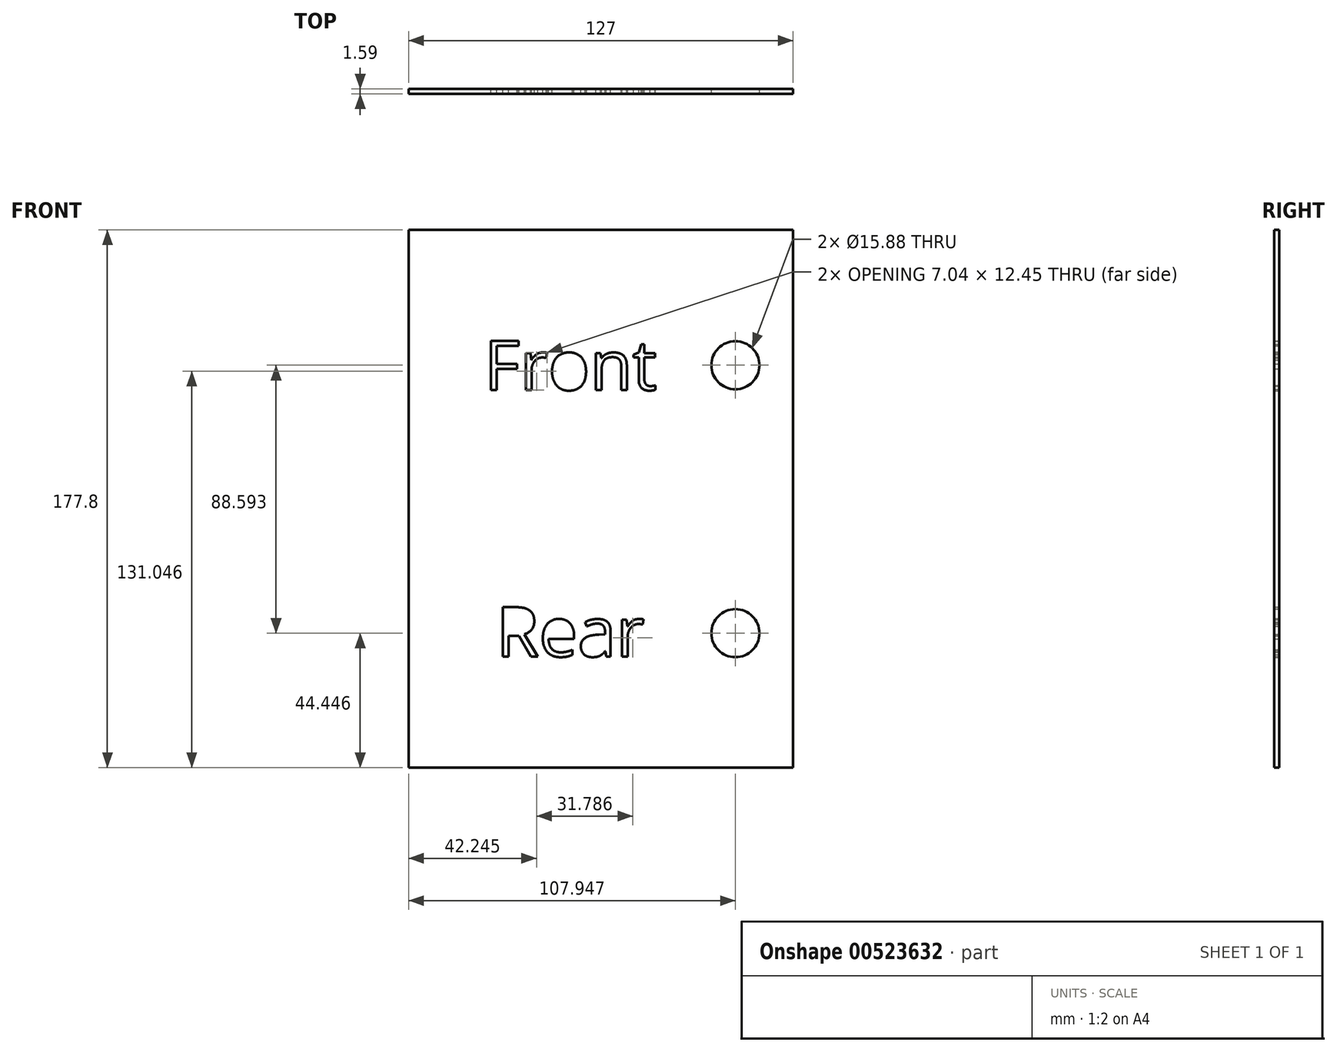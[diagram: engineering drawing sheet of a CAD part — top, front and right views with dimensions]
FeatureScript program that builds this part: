
annotation { "Feature Type Name" : "Feature", "Feature Type Description" : "" }
export const myFeature = defineFeature(function(context is Context, id is Id, definition is map)
    precondition{}
    {
        {
            var Q0;
            Q0=qCreatedBy(makeId("Front.planeOp"),FACE);
            var sketch = newSketch(context, id + "F0", { "sketchPlane" : qUnion([Q0])});
            skLineSegment(sketch, "E0.bottom", {"start": v(-47.7, 65.32) * mm, "end": v(79.3, 65.32) * mm});
            skLineSegment(sketch, "E0.top", {"start": v(-47.7, -112.48) * mm, "end": v(79.3, -112.48) * mm});
            skLineSegment(sketch, "E0.left", {"start": v(-47.7, 65.32) * mm, "end": v(-47.7, -112.48) * mm});
            skLineSegment(sketch, "E0.right", {"start": v(79.3, 65.32) * mm, "end": v(79.3, -112.48) * mm});
            skText(sketch, "E1", { "text": "Front", "fontName": "OpenSans-Regular.ttf"});
            skText(sketch, "E2", { "text": "Rear", "fontName": "OpenSans-Regular.ttf"});
            skCircle(sketch, "E3", {"center": v(60.25, 20.56) * mm, "radius": 7.94 * mm});
            skPoint(sketch, "E3.centerSnap0", {"position": v(-22.73, 20.56) * mm});
            skCircle(sketch, "E4", {"center": v(60.25, -68.03) * mm, "radius": 7.94 * mm});
            skPoint(sketch, "E4.centerSnap0", {"position": v(15.8, -68.03) * mm});
            const initialGuessF0  = {"E1": [-0.02273, 0.01234, 1, 0, 0.01645], "E2": [-0.0188, -0.07577, 1, 0, 0.01645]};
            skSetInitialGuess(sketch, initialGuessF0);
            skSolve(sketch);
        }
        {
            var Q0;
            Q0=makeQuery(id+"F0.imprint","IMPRINT",FACE,{"disambiguationData":[TD([[makeQuery(id+"F0.imprint","IMPRINT",EDGE,{"derivedFrom":sQuery(id+"F0.wireOp",EDGE,"E0.bottom")}),-1.0]])]});
            extrude(context, id + "F1", {"entities" : qUnion([Q0]), "depth" : 1.59 * mm, "offsetDistance" : 25.4 * mm});
        }
    });
